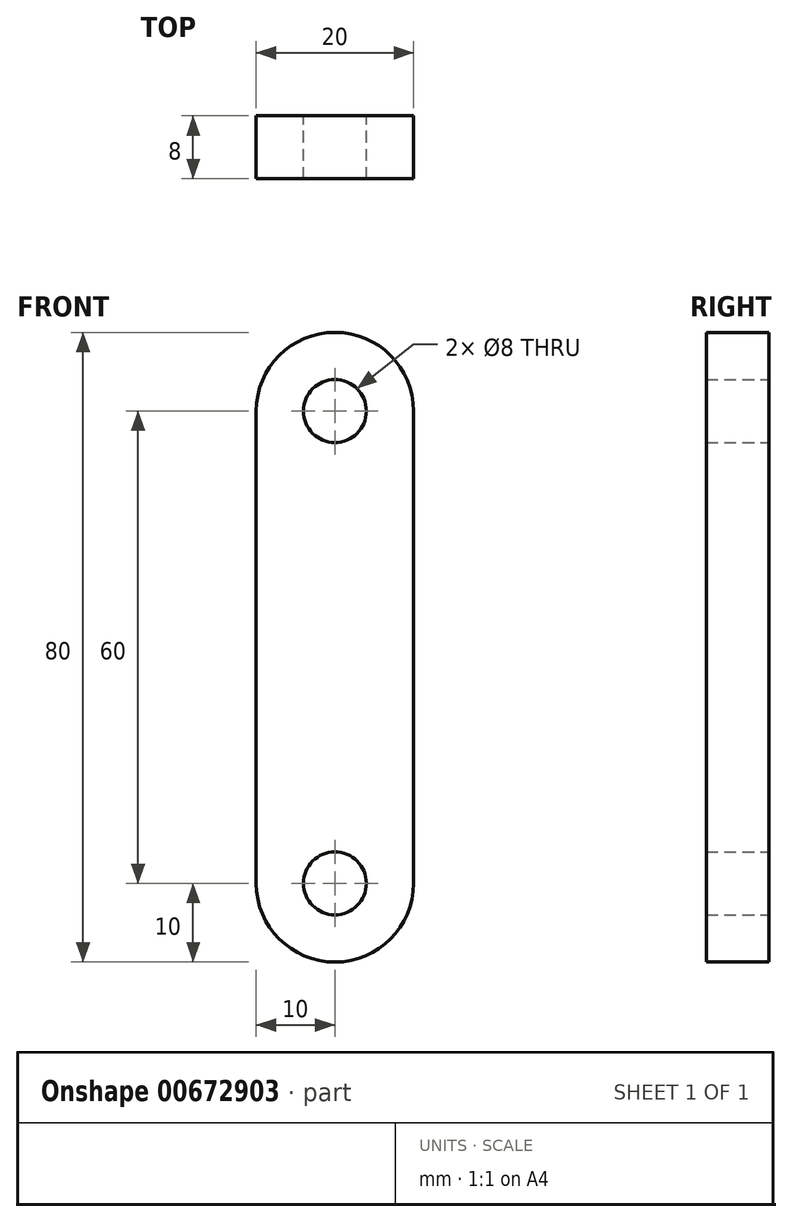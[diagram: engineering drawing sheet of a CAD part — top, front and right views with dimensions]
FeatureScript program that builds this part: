
annotation { "Feature Type Name" : "Feature", "Feature Type Description" : "" }
export const myFeature = defineFeature(function(context is Context, id is Id, definition is map)
    precondition{}
    {
        {
            var Q0;
            Q0=qCreatedBy(makeId("Front.planeOp"),FACE);
            var sketch = newSketch(context, id + "F0", { "sketchPlane" : qUnion([Q0])});
            skArc(sketch, "E0", {"start": v(-10, 0) * mm, "mid": v(0, -10) * mm, "end": v(10, 0) * mm});
            skArc(sketch, "E1", {"start": v(10, 60) * mm, "mid": v(0, 70) * mm, "end": v(-10, 60) * mm});
            skCircle(sketch, "E2", {"center": v(0, 60) * mm, "radius": 4 * mm});
            skCircle(sketch, "E3", {"center": v(0, 0) * mm, "radius": 4 * mm});
            skLineSegment(sketch, "E4", {"start": v(-10, 60) * mm, "end": v(-10, 0) * mm});
            skLineSegment(sketch, "E5", {"start": v(10, 0) * mm, "end": v(10, 60) * mm});
            skSolve(sketch);
        }
        {
            var Q0;
            Q0 = qSketchRegion(id + "F0", true);
            extrude(context, id + "F1", {"entities" : qUnion([Q0]), "depth" : 8 * mm, "offsetDistance" : 25 * mm});
        }
    });
